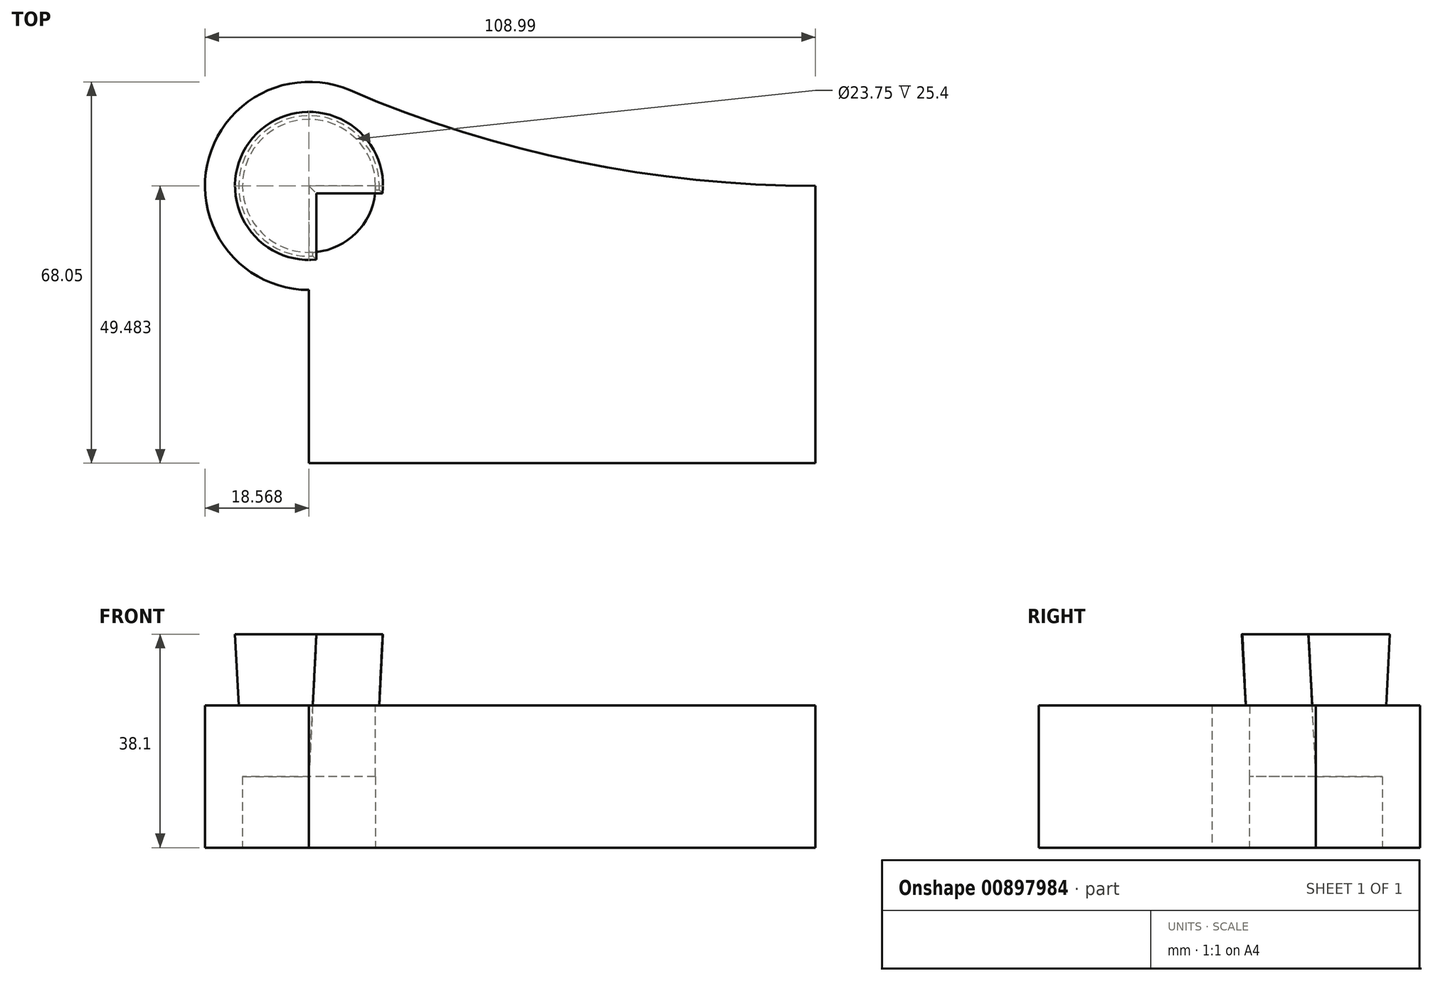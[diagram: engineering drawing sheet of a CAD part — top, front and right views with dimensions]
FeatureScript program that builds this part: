
annotation { "Feature Type Name" : "Feature", "Feature Type Description" : "" }
export const myFeature = defineFeature(function(context is Context, id is Id, definition is map)
    precondition{}
    {
        {
            var Q0;
            Q0=qCreatedBy(makeId("Top.planeOp"),FACE);
            var sketch = newSketch(context, id + "F0", { "sketchPlane" : qUnion([Q0])});
            skLineSegment(sketch, "E0.bottom", {"start": v(45.21, -24.74) * mm, "end": v(-45.21, -24.74) * mm});
            skLineSegment(sketch, "E0.top", {"start": v(45.21, 24.74) * mm, "end": v(-45.21, 24.74) * mm});
            skLineSegment(sketch, "E0.left", {"start": v(45.21, -24.74) * mm, "end": v(45.21, 24.74) * mm});
            skLineSegment(sketch, "E0.right", {"start": v(-45.21, -24.74) * mm, "end": v(-45.21, 24.74) * mm});
            skPoint(sketch, "E0.middle", {"position": v(0, 0) * mm});
            skCircle(sketch, "E1", {"center": v(-45.21, 24.74) * mm, "radius": 18.56 * mm});
            skArc(sketch, "E2", {"start": v(-37.9, 41.8) * mm, "mid": v(2.8, 29.05) * mm, "end": v(45.21, 24.74) * mm});
            skCircle(sketch, "E3", {"center": v(-45.21, 24.74) * mm, "radius": 11.88 * mm});
            skSolve(sketch);
        }
        {
            var Q0;
            {var subQ0=sQuery(id+"F0.wireOp",EDGE,"E1");var subQ4=sQuery(id+"F0.wireOp",EDGE,"E0.top");var subQ5=makeQuery(id+"F0.imprint","INTERSECT",VERTEX,{"derivedFrom":[subQ4,subQ0]});Q0=makeQuery(id+"F0.imprint","IMPRINT",FACE,{"disambiguationData":[TD([[makeQuery(id+"F0.imprint","IMPRINT",EDGE,{"disambiguationData":[TD([[subQ5,-1.0]])],"derivedFrom":subQ4}),-1.0]])]});}
            var Q1;
            {var subQ0=sQuery(id+"F0.wireOp",EDGE,"E2");Q1=makeQuery(id+"F0.imprint","IMPRINT",FACE,{"disambiguationData":[TD([[makeQuery(id+"F0.imprint","IMPRINT",EDGE,{"derivedFrom":subQ0}),-1.0]])]});}
            var Q2;
            {var subQ5=sQuery(id+"F0.wireOp",EDGE,"E0.bottom");Q2=makeQuery(id+"F0.imprint","IMPRINT",FACE,{"disambiguationData":[TD([[makeQuery(id+"F0.imprint","IMPRINT",EDGE,{"derivedFrom":subQ5}),-1.0]])]});}
            var Q3;
            {var subQ0=sQuery(id+"F0.wireOp",EDGE,"E1");var subQ1=sQuery(id+"F0.wireOp",EDGE,"E0.top");var subQ2=makeQuery(id+"F0.imprint","INTERSECT",VERTEX,{"derivedFrom":[subQ1,subQ0]});Q3=makeQuery(id+"F0.imprint","IMPRINT",FACE,{"disambiguationData":[TD([[makeQuery(id+"F0.imprint","IMPRINT",EDGE,{"disambiguationData":[TD([[subQ2,-1.0]])],"derivedFrom":subQ1}),1.0]])]});}
            extrude(context, id + "F1", {"entities" : qUnion([Q0, Q1, Q2, Q3]), "endBound" : BoundingType.SYMMETRIC, "depth" : 25.4 * mm, "offsetDistance" : 25.4 * mm});
        }
        {
            var Q0;
            {var subQ0=sQuery(id+"F0.wireOp",EDGE,"E0.right");var subQ1=sQuery(id+"F0.wireOp",EDGE,"E0.top");var subQ2=makeQuery(id+"F0.imprint","INTERSECT",VERTEX,{"derivedFrom":[subQ1,subQ0]});Q0=makeQuery(id+"F0.imprint","IMPRINT",FACE,{"disambiguationData":[TD([[makeQuery(id+"F0.imprint","IMPRINT",EDGE,{"disambiguationData":[TD([[subQ2,1.0]])],"derivedFrom":subQ1}),-1.0]])]});}
            extrude(context, id + "F2", {"entities" : qUnion([Q0]), "operationType" : NewBodyOperationType.ADD, "depth" : 25.4 * mm, "offsetDistance" : 25.4 * mm, "hasDraft" : true, "draftAngle" : 3 * degree});
        }
        {
            var Q0;
            Q0=makeQuery(id+"F1.opExtrude","SWEPT_FACE",FACE,{"disambiguationData":[OSD([sQuery(id+"F0.wireOp",EDGE,"E0.bottom")])]});
            extrude(context, id + "F3", {"entities" : qUnion([Q0]), "operationType" : NewBodyOperationType.REMOVE, "depth" : 25.4 * mm, "offsetDistance" : 25.4 * mm});
        }
    });
